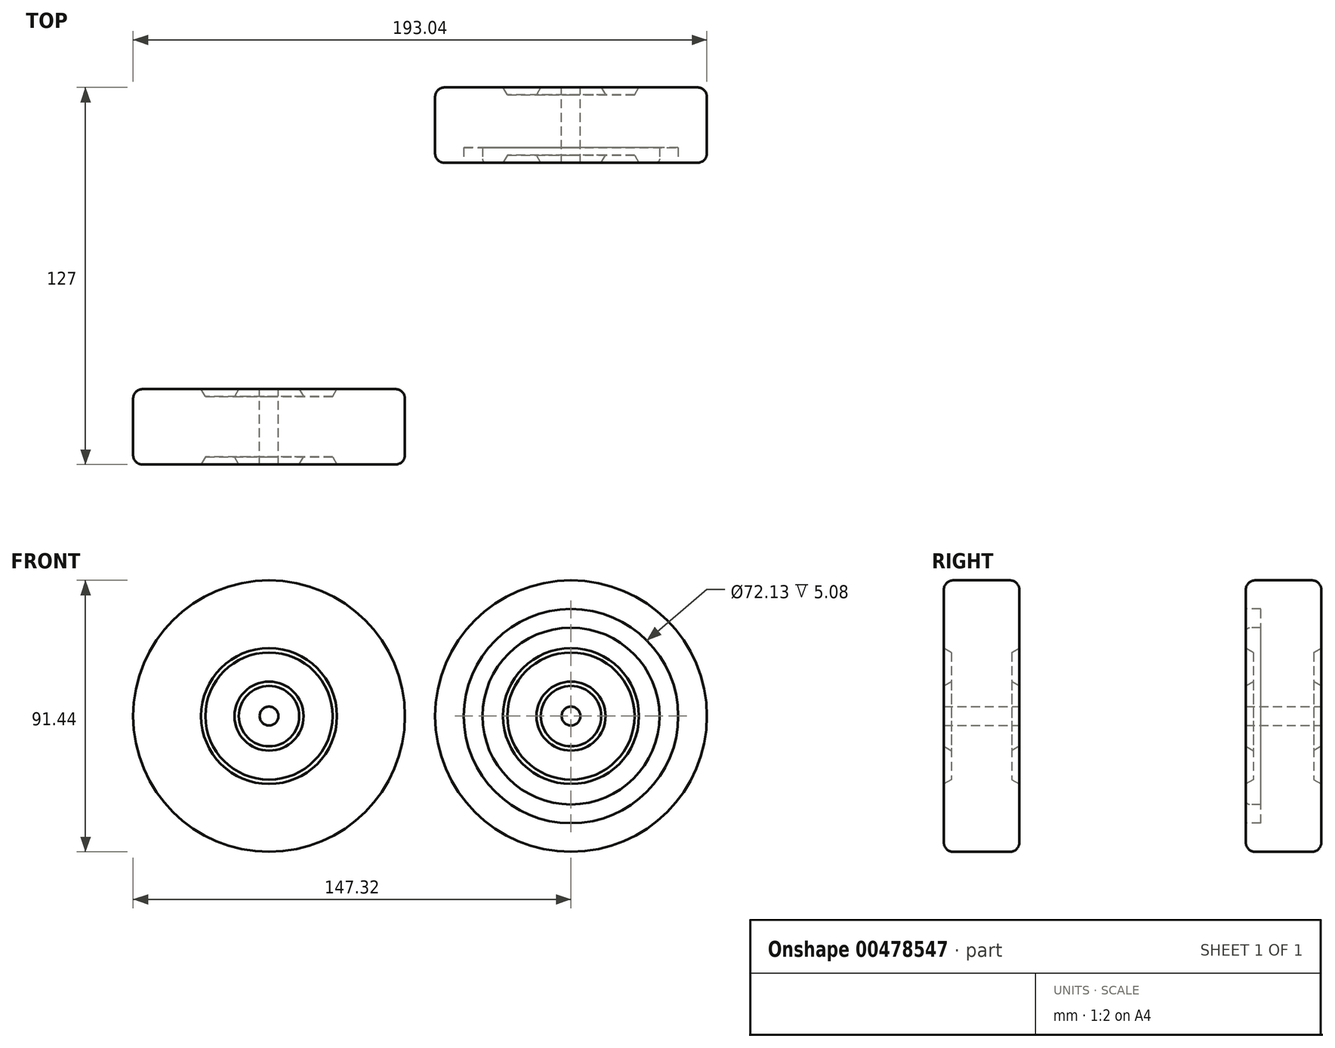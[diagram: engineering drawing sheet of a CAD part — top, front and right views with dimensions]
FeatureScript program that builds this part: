
annotation { "Feature Type Name" : "Feature", "Feature Type Description" : "" }
export const myFeature = defineFeature(function(context is Context, id is Id, definition is map)
    precondition{}
    {
        {
            var Q0;
            Q0=qCreatedBy(makeId("Right.planeOp"),FACE);
            var sketch = newSketch(context, id + "F0", { "sketchPlane" : qUnion([Q0])});
            skLineSegment(sketch, "E0", {"start": v(0, 0) * mm, "end": v(45.88, 0) * mm, "construction": true});
            skLineSegment(sketch, "E1", {"start": v(12.7, 3.18) * mm, "end": v(12.7, 10.16) * mm});
            skLineSegment(sketch, "E2", {"start": v(12.7, 10.16) * mm, "end": v(10.16, 11.63) * mm});
            skLineSegment(sketch, "E3", {"start": v(10.16, 11.63) * mm, "end": v(10.16, 21.4) * mm});
            skLineSegment(sketch, "E4", {"start": v(10.16, 21.4) * mm, "end": v(12.7, 22.86) * mm});
            skLineSegment(sketch, "E5", {"start": v(12.7, 22.86) * mm, "end": v(12.7, 42.55) * mm});
            skLineSegment(sketch, "E6.MirrorCS", {"start": v(-10.16, 21.4) * mm, "end": v(-12.7, 22.86) * mm});
            skLineSegment(sketch, "E7.MirrorCS", {"start": v(-12.7, 10.16) * mm, "end": v(-10.16, 11.63) * mm});
            skLineSegment(sketch, "E8.MirrorCS", {"start": v(-10.16, 11.63) * mm, "end": v(-10.16, 21.4) * mm});
            skLineSegment(sketch, "E9.MirrorCS", {"start": v(0, 0) * mm, "end": v(-45.88, 0) * mm, "construction": true});
            skLineSegment(sketch, "E10.MirrorCS", {"start": v(-12.7, 3.18) * mm, "end": v(-12.7, 10.16) * mm});
            skLineSegment(sketch, "E11.MirrorCS", {"start": v(-12.7, 22.86) * mm, "end": v(-12.7, 42.55) * mm});
            skLineSegment(sketch, "E12", {"start": v(-9.52, 45.72) * mm, "end": v(9.52, 45.72) * mm});
            skPoint(sketch, "E13.visualSharp", {"position": v(-12.7, 45.72) * mm});
            skArc(sketch, "E13.filletArc", {"start": v(-9.52, 45.72) * mm, "mid": v(-11.77, 44.8) * mm, "end": v(-12.7, 42.55) * mm});
            skPoint(sketch, "E14.visualSharp", {"position": v(12.7, 45.72) * mm});
            skArc(sketch, "E14.filletArc", {"start": v(12.7, 42.55) * mm, "mid": v(11.77, 44.8) * mm, "end": v(9.52, 45.72) * mm});
            skLineSegment(sketch, "E15", {"start": v(-12.7, 3.18) * mm, "end": v(12.7, 3.18) * mm});
            skSolve(sketch);
        }
        {
            var Q0;
            Q0=makeQuery(id+"F0.imprint","IMPRINT",FACE,{"disambiguationData":[TD([[makeQuery(id+"F0.imprint","IMPRINT",EDGE,{"derivedFrom":sQuery(id+"F0.wireOp",EDGE,"E1")}),1.0]])]});
            var Q1;
            Q1=sQuery(id+"F0.wireOp",EDGE,"E9.MirrorCS");
            revolve(context, id + "F1", {"entities" : qUnion([Q0]), "axis" : qUnion([Q1]), "revolveType" : RevolveType.FULL});
        }
        {
            var Q0;
            Q0=makeQuery(id+"F1.opRevolve","SWEPT_BODY",BODY,{"disambiguationData":[OSD([sQuery(id+"F0.wireOp",EDGE,"E1"),sQuery(id+"F0.wireOp",EDGE,"E2"),sQuery(id+"F0.wireOp",EDGE,"E3"),sQuery(id+"F0.wireOp",EDGE,"E4"),sQuery(id+"F0.wireOp",EDGE,"E5"),sQuery(id+"F0.wireOp",EDGE,"E6.MirrorCS"),sQuery(id+"F0.wireOp",EDGE,"E7.MirrorCS"),sQuery(id+"F0.wireOp",EDGE,"E8.MirrorCS"),sQuery(id+"F0.wireOp",EDGE,"E10.MirrorCS"),sQuery(id+"F0.wireOp",EDGE,"E11.MirrorCS"),sQuery(id+"F0.wireOp",EDGE,"E12"),sQuery(id+"F0.wireOp",EDGE,"E13.filletArc"),sQuery(id+"F0.wireOp",EDGE,"E14.filletArc"),sQuery(id+"F0.wireOp",EDGE,"E15")])]});
            transform(context, id + "F2", {"entities" : qUnion([Q0]), "transformType" : TransformType.TRANSLATION_3D, "dx" : 0 * mm, "dy" : 0 * mm, "dz" : 0 * mm, "makeCopy" : true});
        }
        {
            var Q0;
            Q0=makeQuery(id+"F1.opRevolve","SWEPT_BODY",BODY,{"disambiguationData":[OSD([sQuery(id+"F0.wireOp",EDGE,"E1"),sQuery(id+"F0.wireOp",EDGE,"E2"),sQuery(id+"F0.wireOp",EDGE,"E3"),sQuery(id+"F0.wireOp",EDGE,"E4"),sQuery(id+"F0.wireOp",EDGE,"E5"),sQuery(id+"F0.wireOp",EDGE,"E6.MirrorCS"),sQuery(id+"F0.wireOp",EDGE,"E7.MirrorCS"),sQuery(id+"F0.wireOp",EDGE,"E8.MirrorCS"),sQuery(id+"F0.wireOp",EDGE,"E10.MirrorCS"),sQuery(id+"F0.wireOp",EDGE,"E11.MirrorCS"),sQuery(id+"F0.wireOp",EDGE,"E12"),sQuery(id+"F0.wireOp",EDGE,"E13.filletArc"),sQuery(id+"F0.wireOp",EDGE,"E14.filletArc"),sQuery(id+"F0.wireOp",EDGE,"E15")])]});
            deleteBodies(context, id + "F3", {"entities" : qUnion([Q0])});
        }
        {
            var Q0;
            Q0=makeQuery(id+"F2.opPattern","COPY",BODY,{"derivedFrom":makeQuery(id+"F1.opRevolve","SWEPT_BODY",BODY,{"disambiguationData":[OSD([sQuery(id+"F0.wireOp",EDGE,"E1"),sQuery(id+"F0.wireOp",EDGE,"E2"),sQuery(id+"F0.wireOp",EDGE,"E3"),sQuery(id+"F0.wireOp",EDGE,"E4"),sQuery(id+"F0.wireOp",EDGE,"E5"),sQuery(id+"F0.wireOp",EDGE,"E6.MirrorCS"),sQuery(id+"F0.wireOp",EDGE,"E7.MirrorCS"),sQuery(id+"F0.wireOp",EDGE,"E8.MirrorCS"),sQuery(id+"F0.wireOp",EDGE,"E10.MirrorCS"),sQuery(id+"F0.wireOp",EDGE,"E11.MirrorCS"),sQuery(id+"F0.wireOp",EDGE,"E12"),sQuery(id+"F0.wireOp",EDGE,"E13.filletArc"),sQuery(id+"F0.wireOp",EDGE,"E14.filletArc"),sQuery(id+"F0.wireOp",EDGE,"E15")])]}),"instanceName":"1"});
            transform(context, id + "F4", {"entities" : qUnion([Q0]), "transformType" : TransformType.TRANSLATION_3D, "dx" : 101.6 * mm, "dy" : 101.6 * mm, "dz" : 0 * mm, "makeCopy" : true});
        }
        {
            var Q0;
            Q0=makeQuery(id+"F4.opPattern","COPY",FACE,{"derivedFrom":makeQuery(id+"F2.opPattern","COPY",FACE,{"derivedFrom":makeQuery(id+"F1.opRevolve","SWEPT_FACE",FACE,{"disambiguationData":[OSD([sQuery(id+"F0.wireOp",EDGE,"E11.MirrorCS")])]}),"instanceName":"1"}),"instanceName":"1"});
            var sketch = newSketch(context, id + "F5", { "sketchPlane" : qUnion([Q0])});
            skCircle(sketch, "E16", {"center": v(101.6, 0) * mm, "radius": 29.76 * mm});
            skCircle(sketch, "E17", {"center": v(101.6, 0) * mm, "radius": 36.06 * mm});
            skSolve(sketch);
        }
        {
            var Q0;
            Q0 = qSketchRegion(id + "F5", true);
            extrude(context, id + "F6", {"entities" : qUnion([Q0]), "operationType" : NewBodyOperationType.REMOVE, "oppositeDirection" : true, "depth" : 5.08 * mm});
        }
        {
            var Q0;
            Q0=makeQuery(id+"F6.boolean.opBoolean","COPY",EDGE,{"derivedFrom":makeQuery(id+"F6.opExtrude","CAP_EDGE",EDGE,{"disambiguationData":[OSD([sQuery(id+"F5.wireOp",EDGE,"E17")])],"isStart":true})});
            var Q1;
            Q1=makeQuery(id+"F6.boolean.opBoolean","COPY",EDGE,{"derivedFrom":makeQuery(id+"F6.opExtrude","CAP_EDGE",EDGE,{"disambiguationData":[OSD([sQuery(id+"F5.wireOp",EDGE,"E16")])],"isStart":true})});
            fillet(context, id + "F7", {"entities" : qUnion([Q0, Q1]), "radius" : 1.27 * mm, "tangentPropagation" : true, "allowEdgeOverflow" : false});
        }
    });
